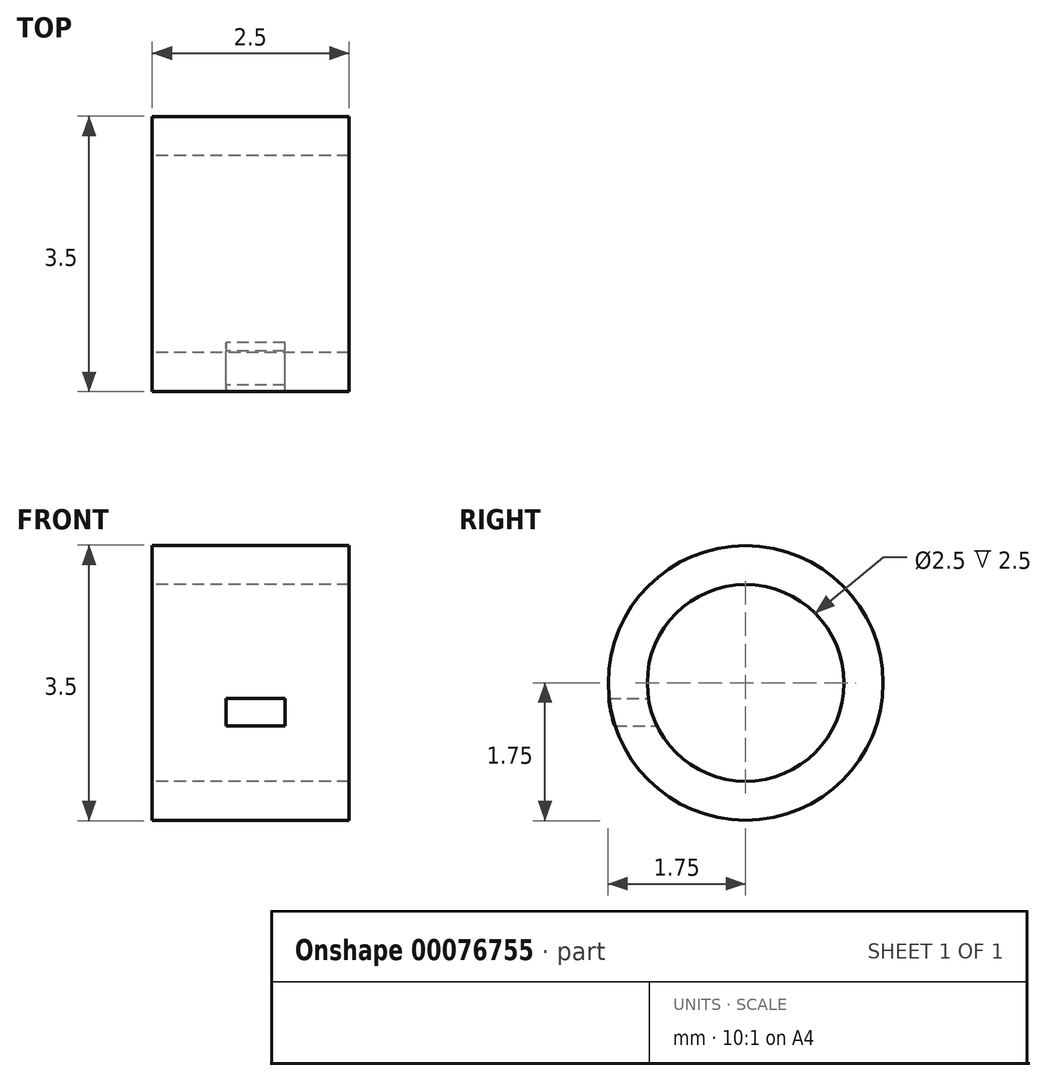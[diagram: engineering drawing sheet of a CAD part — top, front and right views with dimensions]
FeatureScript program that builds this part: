
annotation { "Feature Type Name" : "Feature", "Feature Type Description" : "" }
export const myFeature = defineFeature(function(context is Context, id is Id, definition is map)
    precondition{}
    {
        {
            var Q0;
            Q0=qCreatedBy(makeId("Right.planeOp"),FACE);
            var sketch = newSketch(context, id + "F0", { "sketchPlane" : qUnion([Q0])});
            skCircle(sketch, "E0", {"center": v(0, 0) * mm, "radius": 1.25 * mm});
            skCircle(sketch, "E1", {"center": v(0, 0) * mm, "radius": 1.75 * mm});
            skSolve(sketch);
        }
        {
            var Q0;
            Q0=makeQuery(id+"F0.imprint","IMPRINT",FACE,{"disambiguationData":[TD([[makeQuery(id+"F0.imprint","IMPRINT",EDGE,{"derivedFrom":sQuery(id+"F0.wireOp",EDGE,"E0")}),-1.0]])]});
            var Q1;
            Q1=makeQuery(id+"F0.imprint","IMPRINT",FACE,{"disambiguationData":[TD([[makeQuery(id+"F0.imprint","IMPRINT",EDGE,{"derivedFrom":sQuery(id+"F0.wireOp",EDGE,"E1")}),1.0]])]});
            extrude(context, id + "F1", {"entities" : qUnion([Q0, Q1]), "depth" : 2.5 * mm});
        }
        {
            var Q0;
            Q0=qCreatedBy(makeId("Front.planeOp"),FACE);
            var sketch = newSketch(context, id + "F2", { "sketchPlane" : qUnion([Q0])});
            skText(sketch, "E2", { "text": "-", "fontName": "OpenSans-Bold.ttf"});
            const initialGuessF2  = {"E2": [0.00085, -0.00114, 1, 0, 0.00206]};
            skSetInitialGuess(sketch, initialGuessF2);
            skSolve(sketch);
        }
        {
            var Q0;
            Q0=qSketchRegion(id+"F2",true);
            var Q1;
            Q1=qConstructionFilter(qBodyType(qCreatedBy(id+"F2",EDGE),BodyType.WIRE),ConstructionObject.NO);
            var Q2;
            Q2=makeQuery(id+"F1.opExtrude","SWEPT_FACE",FACE,{"disambiguationData":[OSD([sQuery(id+"F0.wireOp",EDGE,"E1")])]});
            var Q3;
            Q3=makeQuery(id+"F1.opExtrude","SWEPT_BODY",BODY,{"disambiguationData":[OSD([sQuery(id+"F0.wireOp",EDGE,"E0"),sQuery(id+"F0.wireOp",EDGE,"E1")])]});
            var Q4;
            Q4=sQuery(id+"F0.wireOp",VERTEX,"27635d6e-dcd6-4653-b727-4819003c0945");
            extrude(context, id + "F3", {"entities" : qUnion([Q0]), "operationType" : NewBodyOperationType.INTERSECT, "surfaceEntities" : qUnion([Q1]), "endBound" : BoundingType.UP_TO_SURFACE, "endBoundEntityFace" : qUnion([Q2]), "endBoundEntityBody" : qUnion([Q3]), "endBoundEntityVertex" : qUnion([Q4]), "depth" : 25 * mm});
        }
        {
            var Q0;
            Q0=makeQuery(id+"F0.imprint","IMPRINT",FACE,{"disambiguationData":[TD([[makeQuery(id+"F0.imprint","IMPRINT",EDGE,{"derivedFrom":sQuery(id+"F0.wireOp",EDGE,"E0")}),-1.0]])]});
            extrude(context, id + "F4", {"entities" : qUnion([Q0]), "depth" : 2.5 * mm});
        }
    });
